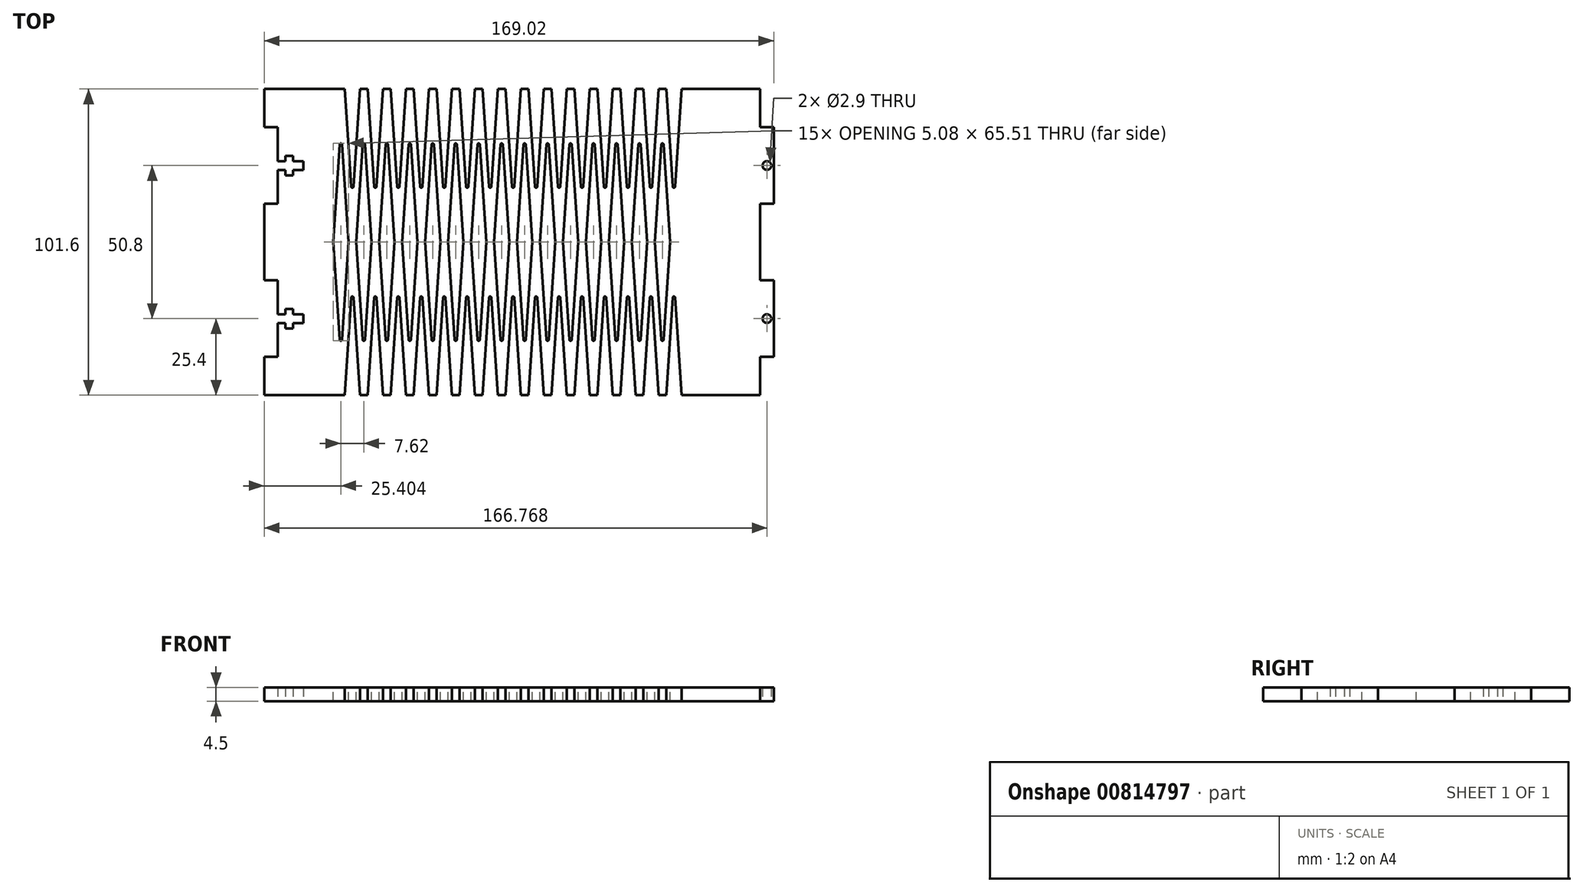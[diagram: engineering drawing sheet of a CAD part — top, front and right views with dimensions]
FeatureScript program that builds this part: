
annotation { "Feature Type Name" : "Feature", "Feature Type Description" : "" }
export const myFeature = defineFeature(function(context is Context, id is Id, definition is map)
    precondition{}
    {
        {
            var Q0;
            Q0=qCreatedBy(makeId("Top.planeOp"),FACE);
            var sketch = newSketch(context, id + "F0", { "sketchPlane" : qUnion([Q0])});
            skLineSegment(sketch, "E0.bottom", {"start": v(-80, 50.8) * mm, "end": v(80.01, 50.8) * mm});
            skLineSegment(sketch, "E0.top", {"start": v(-80, -50.8) * mm, "end": v(80.01, -50.8) * mm});
            skLineSegment(sketch, "E1", {"start": v(-80.01, 50.8) * mm, "end": v(80.01, -50.8) * mm, "construction": true});
            skLineSegment(sketch, "E2.left", {"start": v(-80, 38.1) * mm, "end": v(-80, 26.85) * mm});
            skLineSegment(sketch, "E3", {"start": v(-80, 50.8) * mm, "end": v(-84.5, 50.8) * mm});
            skLineSegment(sketch, "E4", {"start": v(-84.5, 50.8) * mm, "end": v(-84.5, 38.1) * mm});
            skLineSegment(sketch, "E5", {"start": v(-84.5, 38.1) * mm, "end": v(-80, 38.1) * mm});
            skLineSegment(sketch, "E6", {"start": v(-80, 12.7) * mm, "end": v(-84.5, 12.7) * mm});
            skLineSegment(sketch, "E7", {"start": v(-84.5, 12.7) * mm, "end": v(-84.5, 0) * mm});
            skLineSegment(sketch, "E8", {"start": v(-80, 26.85) * mm, "end": v(-77.47, 26.85) * mm});
            skLineSegment(sketch, "E9", {"start": v(-77.47, 26.85) * mm, "end": v(-77.47, 28.64) * mm});
            skLineSegment(sketch, "E10", {"start": v(-77.47, 28.64) * mm, "end": v(-74.96, 28.64) * mm});
            skLineSegment(sketch, "E11", {"start": v(-74.96, 28.64) * mm, "end": v(-74.96, 26.85) * mm});
            skLineSegment(sketch, "E12", {"start": v(-74.96, 26.85) * mm, "end": v(-71.55, 26.85) * mm});
            skLineSegment(sketch, "E13", {"start": v(-71.55, 26.85) * mm, "end": v(-71.55, 23.95) * mm});
            skLineSegment(sketch, "E14", {"start": v(-71.55, 23.95) * mm, "end": v(-74.96, 23.95) * mm});
            skLineSegment(sketch, "E15", {"start": v(-74.96, 23.95) * mm, "end": v(-74.96, 22.16) * mm});
            skLineSegment(sketch, "E16", {"start": v(-74.96, 22.16) * mm, "end": v(-77.47, 22.16) * mm});
            skLineSegment(sketch, "E17", {"start": v(-77.47, 22.16) * mm, "end": v(-77.47, 23.95) * mm});
            skLineSegment(sketch, "E18", {"start": v(-77.47, 23.95) * mm, "end": v(-80, 23.95) * mm});
            skLineSegment(sketch, "E19", {"start": v(-77.47, 26.85) * mm, "end": v(-77.47, 23.95) * mm, "construction": true});
            skLineSegment(sketch, "E20", {"start": v(-74.96, 26.85) * mm, "end": v(-74.96, 23.95) * mm, "construction": true});
            skLineSegment(sketch, "E21", {"start": v(-71.55, 25.4) * mm, "end": v(-80, 25.4) * mm, "construction": true});
            skPoint(sketch, "E21.endSnap0", {"position": v(-74.96, 25.4) * mm});
            skLineSegment(sketch, "E22", {"start": v(-80, 23.95) * mm, "end": v(-80, 12.7) * mm});
            skLineSegment(sketch, "E23", {"start": v(-80, 23.95) * mm, "end": v(-80, 26.85) * mm, "construction": true});
            skLineSegment(sketch, "E24", {"start": v(0, 0) * mm, "end": v(-84.5, 0) * mm, "construction": true});
            skLineSegment(sketch, "E25.MirrorCS", {"start": v(-77.47, -26.85) * mm, "end": v(-77.47, -28.64) * mm});
            skLineSegment(sketch, "E26.MirrorCS", {"start": v(-77.47, -28.64) * mm, "end": v(-74.96, -28.64) * mm});
            skLineSegment(sketch, "E27.MirrorCS", {"start": v(-74.96, -28.64) * mm, "end": v(-74.96, -26.85) * mm});
            skLineSegment(sketch, "E28.MirrorCS", {"start": v(-80, -26.85) * mm, "end": v(-77.47, -26.85) * mm});
            skLineSegment(sketch, "E29.MirrorCS", {"start": v(-71.55, -23.95) * mm, "end": v(-74.96, -23.95) * mm});
            skLineSegment(sketch, "E30.MirrorCS", {"start": v(-74.96, -26.85) * mm, "end": v(-74.96, -23.95) * mm, "construction": true});
            skLineSegment(sketch, "E31.MirrorCS", {"start": v(-77.47, -23.95) * mm, "end": v(-80, -23.95) * mm});
            skLineSegment(sketch, "E32.MirrorCS", {"start": v(-71.55, -25.4) * mm, "end": v(-80, -25.4) * mm, "construction": true});
            skLineSegment(sketch, "E33.MirrorCS", {"start": v(-74.96, -23.95) * mm, "end": v(-74.96, -22.16) * mm});
            skLineSegment(sketch, "E34.MirrorCS", {"start": v(-77.47, -22.16) * mm, "end": v(-77.47, -23.95) * mm});
            skLineSegment(sketch, "E35.MirrorCS", {"start": v(-80, -23.95) * mm, "end": v(-80, -26.85) * mm, "construction": true});
            skLineSegment(sketch, "E36.MirrorCS", {"start": v(-77.47, -26.85) * mm, "end": v(-77.47, -23.95) * mm, "construction": true});
            skLineSegment(sketch, "E37.MirrorCS", {"start": v(-74.96, -26.85) * mm, "end": v(-71.55, -26.85) * mm});
            skLineSegment(sketch, "E38.MirrorCS", {"start": v(-71.55, -26.85) * mm, "end": v(-71.55, -23.95) * mm});
            skLineSegment(sketch, "E39.MirrorCS", {"start": v(-74.96, -22.16) * mm, "end": v(-77.47, -22.16) * mm});
            skLineSegment(sketch, "E40.MirrorCS", {"start": v(-80, -12.7) * mm, "end": v(-84.5, -12.7) * mm});
            skLineSegment(sketch, "E41.MirrorCS", {"start": v(-84.5, -38.1) * mm, "end": v(-80, -38.1) * mm});
            skLineSegment(sketch, "E42.MirrorCS", {"start": v(-80, -50.8) * mm, "end": v(-84.5, -50.8) * mm});
            skLineSegment(sketch, "E43.MirrorCS", {"start": v(-84.5, -12.7) * mm, "end": v(-84.5, 0) * mm});
            skLineSegment(sketch, "E44.MirrorCS", {"start": v(-80, -23.95) * mm, "end": v(-80, -12.7) * mm});
            skPoint(sketch, "E45.MirrorP", {"position": v(-74.96, -25.4) * mm});
            skLineSegment(sketch, "E46.MirrorCS", {"start": v(-84.5, -50.8) * mm, "end": v(-84.5, -38.1) * mm});
            skLineSegment(sketch, "E47.MirrorCS", {"start": v(-80, -38.1) * mm, "end": v(-80, -26.85) * mm});
            skLineSegment(sketch, "E48.MirrorCS", {"start": v(80.01, 50.8) * mm, "end": v(80.01, 38.1) * mm});
            skLineSegment(sketch, "E49", {"start": v(80.01, 38.1) * mm, "end": v(84.5, 38.1) * mm});
            skLineSegment(sketch, "E50", {"start": v(84.5, 38.1) * mm, "end": v(84.5, 12.7) * mm});
            skLineSegment(sketch, "E51", {"start": v(84.5, 12.7) * mm, "end": v(80.01, 12.7) * mm});
            skLineSegment(sketch, "E52", {"start": v(80.01, 12.7) * mm, "end": v(80.01, 0) * mm});
            skCircle(sketch, "E53", {"center": v(82.26, 25.4) * mm, "radius": 1.45 * mm});
            skPoint(sketch, "E53.centerSnap0", {"position": v(84.5, 25.4) * mm});
            skLineSegment(sketch, "E54", {"start": v(0, 0) * mm, "end": v(80, 0) * mm, "construction": true});
            skLineSegment(sketch, "E55", {"start": v(84.5, 38.1) * mm, "end": v(80.01, 12.7) * mm, "construction": true});
            skLineSegment(sketch, "E56.MirrorCS", {"start": v(80.01, -38.1) * mm, "end": v(84.5, -38.1) * mm});
            skLineSegment(sketch, "E57.MirrorCS", {"start": v(84.5, -12.7) * mm, "end": v(80.01, -12.7) * mm});
            skCircle(sketch, "E58.MirrorC", {"center": v(82.26, -25.4) * mm, "radius": 1.45 * mm});
            skLineSegment(sketch, "E59.MirrorCS", {"start": v(80.01, -12.7) * mm, "end": v(80.01, 0) * mm});
            skLineSegment(sketch, "E60.MirrorCS", {"start": v(80.01, -50.8) * mm, "end": v(80.01, -38.1) * mm});
            skPoint(sketch, "E61.MirrorP", {"position": v(84.5, -25.4) * mm});
            skLineSegment(sketch, "E62.MirrorCS", {"start": v(84.5, -38.1) * mm, "end": v(84.5, -12.7) * mm});
            skSolve(sketch);
        }
        {
            var Q0;
            Q0 = qSketchRegion(id + "F0", true);
            extrude(context, id + "F1", {"entities" : qUnion([Q0]), "depth" : 4.5 * mm, "offsetDistance" : 25.4 * mm});
        }
        {
            var Q0;
            Q0=makeQuery(id+"F1.opExtrude","CAP_FACE",FACE,{"disambiguationData":[OSD([sQuery(id+"F0.wireOp",EDGE,"E0.bottom"),sQuery(id+"F0.wireOp",EDGE,"E0.top"),sQuery(id+"F0.wireOp",EDGE,"E2.left"),sQuery(id+"F0.wireOp",EDGE,"E3"),sQuery(id+"F0.wireOp",EDGE,"E4"),sQuery(id+"F0.wireOp",EDGE,"E5"),sQuery(id+"F0.wireOp",EDGE,"E6"),sQuery(id+"F0.wireOp",EDGE,"E7"),sQuery(id+"F0.wireOp",EDGE,"E8"),sQuery(id+"F0.wireOp",EDGE,"E9"),sQuery(id+"F0.wireOp",EDGE,"E10"),sQuery(id+"F0.wireOp",EDGE,"E11"),sQuery(id+"F0.wireOp",EDGE,"E12"),sQuery(id+"F0.wireOp",EDGE,"E13"),sQuery(id+"F0.wireOp",EDGE,"E14"),sQuery(id+"F0.wireOp",EDGE,"E15"),sQuery(id+"F0.wireOp",EDGE,"E16"),sQuery(id+"F0.wireOp",EDGE,"E17"),sQuery(id+"F0.wireOp",EDGE,"E18"),sQuery(id+"F0.wireOp",EDGE,"E22"),sQuery(id+"F0.wireOp",EDGE,"E25.MirrorCS"),sQuery(id+"F0.wireOp",EDGE,"E26.MirrorCS"),sQuery(id+"F0.wireOp",EDGE,"E27.MirrorCS"),sQuery(id+"F0.wireOp",EDGE,"E28.MirrorCS"),sQuery(id+"F0.wireOp",EDGE,"E29.MirrorCS"),sQuery(id+"F0.wireOp",EDGE,"E31.MirrorCS"),sQuery(id+"F0.wireOp",EDGE,"E33.MirrorCS"),sQuery(id+"F0.wireOp",EDGE,"E34.MirrorCS"),sQuery(id+"F0.wireOp",EDGE,"E37.MirrorCS"),sQuery(id+"F0.wireOp",EDGE,"E38.MirrorCS"),sQuery(id+"F0.wireOp",EDGE,"E39.MirrorCS"),sQuery(id+"F0.wireOp",EDGE,"E40.MirrorCS"),sQuery(id+"F0.wireOp",EDGE,"E41.MirrorCS"),sQuery(id+"F0.wireOp",EDGE,"E42.MirrorCS"),sQuery(id+"F0.wireOp",EDGE,"E43.MirrorCS"),sQuery(id+"F0.wireOp",EDGE,"E44.MirrorCS"),sQuery(id+"F0.wireOp",EDGE,"E46.MirrorCS"),sQuery(id+"F0.wireOp",EDGE,"E47.MirrorCS"),sQuery(id+"F0.wireOp",EDGE,"E48.MirrorCS"),sQuery(id+"F0.wireOp",EDGE,"E49"),sQuery(id+"F0.wireOp",EDGE,"E50"),sQuery(id+"F0.wireOp",EDGE,"E51"),sQuery(id+"F0.wireOp",EDGE,"E52"),sQuery(id+"F0.wireOp",EDGE,"E53"),sQuery(id+"F0.wireOp",EDGE,"E56.MirrorCS"),sQuery(id+"F0.wireOp",EDGE,"E57.MirrorCS"),sQuery(id+"F0.wireOp",EDGE,"E58.MirrorC"),sQuery(id+"F0.wireOp",EDGE,"E59.MirrorCS"),sQuery(id+"F0.wireOp",EDGE,"E60.MirrorCS"),sQuery(id+"F0.wireOp",EDGE,"E62.MirrorCS")])],"isStart":false});
            var sketch = newSketch(context, id + "F2", { "sketchPlane" : qUnion([Q0])});
            skLineSegment(sketch, "E63", {"start": v(-59.49, 32.4) * mm, "end": v(-61.65, 0) * mm});
            skLineSegment(sketch, "E64", {"start": v(-61.65, 0) * mm, "end": v(-56.57, 0) * mm, "construction": true});
            skLineSegment(sketch, "E65", {"start": v(-56.57, 0) * mm, "end": v(-58.73, 32.4) * mm});
            skLineSegment(sketch, "E66", {"start": v(-57.84, 50.8) * mm, "end": v(-55.68, 18.4) * mm});
            skLineSegment(sketch, "E67", {"start": v(-54.92, 18.4) * mm, "end": v(-52.76, 50.8) * mm});
            skLineSegment(sketch, "E68", {"start": v(-52.76, 50.8) * mm, "end": v(-57.84, 50.8) * mm});
            skLineSegment(sketch, "E69", {"start": v(-59.1, 38.1) * mm, "end": v(-59.1, 0) * mm, "construction": true});
            skLineSegment(sketch, "E70", {"start": v(-55.3, 12.7) * mm, "end": v(-55.3, 50.8) * mm, "construction": true});
            skPoint(sketch, "E71.visualSharp", {"position": v(-59.1, 38.1) * mm});
            skArc(sketch, "E71.filletArc", {"start": v(-58.73, 32.4) * mm, "mid": v(-59.1, 32.75) * mm, "end": v(-59.49, 32.4) * mm});
            skPoint(sketch, "E72.visualSharp", {"position": v(-55.3, 12.7) * mm});
            skArc(sketch, "E72.filletArc", {"start": v(-55.68, 18.4) * mm, "mid": v(-55.3, 18.05) * mm, "end": v(-54.92, 18.4) * mm});
            skArc(sketch, "E73.MirrorCS", {"start": v(-55.68, -18.4) * mm, "mid": v(-55.3, -18.05) * mm, "end": v(-54.92, -18.4) * mm});
            skArc(sketch, "E74.MirrorCS", {"start": v(-58.73, -32.4) * mm, "mid": v(-59.1, -32.75) * mm, "end": v(-59.49, -32.4) * mm});
            skLineSegment(sketch, "E75.MirrorCS", {"start": v(-52.76, -50.8) * mm, "end": v(-57.84, -50.8) * mm});
            skLineSegment(sketch, "E76.MirrorCS", {"start": v(-57.84, -50.8) * mm, "end": v(-55.68, -18.4) * mm});
            skLineSegment(sketch, "E77.MirrorCS", {"start": v(-56.57, 0) * mm, "end": v(-58.73, -32.4) * mm});
            skPoint(sketch, "E78.MirrorP", {"position": v(-59.1, -38.1) * mm});
            skLineSegment(sketch, "E79.MirrorCS", {"start": v(-54.92, -18.4) * mm, "end": v(-52.76, -50.8) * mm});
            skPoint(sketch, "E80.MirrorP", {"position": v(-55.3, -12.7) * mm});
            skLineSegment(sketch, "E81.MirrorCS", {"start": v(-59.49, -32.4) * mm, "end": v(-61.65, 0) * mm});
            skLineSegment(sketch, "E82.1.0.0", {"start": v(-51.87, -32.4) * mm, "end": v(-54.03, 0) * mm});
            skPoint(sketch, "E82.1.0.1", {"position": v(-47.68, -12.7) * mm});
            skPoint(sketch, "E82.1.0.2", {"position": v(-51.49, -38.1) * mm});
            skLineSegment(sketch, "E82.1.0.3", {"start": v(-50.22, 50.8) * mm, "end": v(-48.06, 18.4) * mm});
            skLineSegment(sketch, "E82.1.0.4", {"start": v(-47.3, -18.4) * mm, "end": v(-45.14, -50.8) * mm});
            skLineSegment(sketch, "E82.1.0.5", {"start": v(-48.95, 0) * mm, "end": v(-51.1, -32.4) * mm});
            skPoint(sketch, "E82.1.0.6", {"position": v(-51.49, 38.1) * mm});
            skLineSegment(sketch, "E82.1.0.7", {"start": v(-48.95, 0) * mm, "end": v(-51.1, 32.4) * mm});
            skLineSegment(sketch, "E82.1.0.8", {"start": v(-51.49, 38.1) * mm, "end": v(-51.49, 0) * mm, "construction": true});
            skLineSegment(sketch, "E82.1.0.9", {"start": v(-47.3, 18.4) * mm, "end": v(-45.14, 50.8) * mm});
            skLineSegment(sketch, "E82.1.0.10", {"start": v(-51.87, 32.4) * mm, "end": v(-54.03, 0) * mm});
            skPoint(sketch, "E82.1.0.11", {"position": v(-47.68, 12.7) * mm});
            skLineSegment(sketch, "E82.1.0.12", {"start": v(-47.68, 12.7) * mm, "end": v(-47.68, 50.8) * mm, "construction": true});
            skLineSegment(sketch, "E82.1.0.13", {"start": v(-50.22, -50.8) * mm, "end": v(-48.06, -18.4) * mm});
            skLineSegment(sketch, "E82.1.0.14", {"start": v(-45.14, -50.8) * mm, "end": v(-50.22, -50.8) * mm});
            skArc(sketch, "E82.1.0.15", {"start": v(-48.06, -18.4) * mm, "mid": v(-47.68, -18.05) * mm, "end": v(-47.3, -18.4) * mm});
            skLineSegment(sketch, "E82.1.0.16", {"start": v(-54.03, 0) * mm, "end": v(-48.95, 0) * mm, "construction": true});
            skLineSegment(sketch, "E82.1.0.17", {"start": v(-45.14, 50.8) * mm, "end": v(-50.22, 50.8) * mm});
            skArc(sketch, "E82.1.0.18", {"start": v(-48.06, 18.4) * mm, "mid": v(-47.68, 18.05) * mm, "end": v(-47.3, 18.4) * mm});
            skArc(sketch, "E82.1.0.19", {"start": v(-51.1, -32.4) * mm, "mid": v(-51.49, -32.75) * mm, "end": v(-51.87, -32.4) * mm});
            skArc(sketch, "E82.1.0.20", {"start": v(-51.1, 32.4) * mm, "mid": v(-51.49, 32.75) * mm, "end": v(-51.87, 32.4) * mm});
            skLineSegment(sketch, "E82.2.0.0", {"start": v(-44.25, -32.4) * mm, "end": v(-46.4, 0) * mm});
            skPoint(sketch, "E82.2.0.1", {"position": v(-40.06, -12.7) * mm});
            skPoint(sketch, "E82.2.0.2", {"position": v(-43.87, -38.1) * mm});
            skLineSegment(sketch, "E82.2.0.3", {"start": v(-42.6, 50.8) * mm, "end": v(-40.44, 18.4) * mm});
            skLineSegment(sketch, "E82.2.0.4", {"start": v(-39.68, -18.4) * mm, "end": v(-37.52, -50.8) * mm});
            skLineSegment(sketch, "E82.2.0.5", {"start": v(-41.33, 0) * mm, "end": v(-43.49, -32.4) * mm});
            skPoint(sketch, "E82.2.0.6", {"position": v(-43.87, 38.1) * mm});
            skLineSegment(sketch, "E82.2.0.7", {"start": v(-41.33, 0) * mm, "end": v(-43.49, 32.4) * mm});
            skLineSegment(sketch, "E82.2.0.8", {"start": v(-43.87, 38.1) * mm, "end": v(-43.87, 0) * mm, "construction": true});
            skLineSegment(sketch, "E82.2.0.9", {"start": v(-39.68, 18.4) * mm, "end": v(-37.52, 50.8) * mm});
            skLineSegment(sketch, "E82.2.0.10", {"start": v(-44.25, 32.4) * mm, "end": v(-46.4, 0) * mm});
            skPoint(sketch, "E82.2.0.11", {"position": v(-40.06, 12.7) * mm});
            skLineSegment(sketch, "E82.2.0.12", {"start": v(-40.06, 12.7) * mm, "end": v(-40.06, 50.8) * mm, "construction": true});
            skLineSegment(sketch, "E82.2.0.13", {"start": v(-42.6, -50.8) * mm, "end": v(-40.44, -18.4) * mm});
            skLineSegment(sketch, "E82.2.0.14", {"start": v(-37.52, -50.8) * mm, "end": v(-42.6, -50.8) * mm});
            skArc(sketch, "E82.2.0.15", {"start": v(-40.44, -18.4) * mm, "mid": v(-40.06, -18.05) * mm, "end": v(-39.68, -18.4) * mm});
            skLineSegment(sketch, "E82.2.0.16", {"start": v(-46.4, 0) * mm, "end": v(-41.33, 0) * mm, "construction": true});
            skLineSegment(sketch, "E82.2.0.17", {"start": v(-37.52, 50.8) * mm, "end": v(-42.6, 50.8) * mm});
            skArc(sketch, "E82.2.0.18", {"start": v(-40.44, 18.4) * mm, "mid": v(-40.06, 18.05) * mm, "end": v(-39.68, 18.4) * mm});
            skArc(sketch, "E82.2.0.19", {"start": v(-43.49, -32.4) * mm, "mid": v(-43.87, -32.75) * mm, "end": v(-44.25, -32.4) * mm});
            skArc(sketch, "E82.2.0.20", {"start": v(-43.49, 32.4) * mm, "mid": v(-43.87, 32.75) * mm, "end": v(-44.25, 32.4) * mm});
            skLineSegment(sketch, "E82.3.0.0", {"start": v(-36.63, -32.4) * mm, "end": v(-38.79, 0) * mm});
            skPoint(sketch, "E82.3.0.1", {"position": v(-32.44, -12.7) * mm});
            skPoint(sketch, "E82.3.0.2", {"position": v(-36.25, -38.1) * mm});
            skLineSegment(sketch, "E82.3.0.3", {"start": v(-34.98, 50.8) * mm, "end": v(-32.82, 18.4) * mm});
            skLineSegment(sketch, "E82.3.0.4", {"start": v(-32.06, -18.4) * mm, "end": v(-29.9, -50.8) * mm});
            skLineSegment(sketch, "E82.3.0.5", {"start": v(-33.7, 0) * mm, "end": v(-35.87, -32.4) * mm});
            skPoint(sketch, "E82.3.0.6", {"position": v(-36.25, 38.1) * mm});
            skLineSegment(sketch, "E82.3.0.7", {"start": v(-33.7, 0) * mm, "end": v(-35.87, 32.4) * mm});
            skLineSegment(sketch, "E82.3.0.8", {"start": v(-36.25, 38.1) * mm, "end": v(-36.25, 0) * mm, "construction": true});
            skLineSegment(sketch, "E82.3.0.9", {"start": v(-32.06, 18.4) * mm, "end": v(-29.9, 50.8) * mm});
            skLineSegment(sketch, "E82.3.0.10", {"start": v(-36.63, 32.4) * mm, "end": v(-38.79, 0) * mm});
            skPoint(sketch, "E82.3.0.11", {"position": v(-32.44, 12.7) * mm});
            skLineSegment(sketch, "E82.3.0.12", {"start": v(-32.44, 12.7) * mm, "end": v(-32.44, 50.8) * mm, "construction": true});
            skLineSegment(sketch, "E82.3.0.13", {"start": v(-34.98, -50.8) * mm, "end": v(-32.82, -18.4) * mm});
            skLineSegment(sketch, "E82.3.0.14", {"start": v(-29.9, -50.8) * mm, "end": v(-34.98, -50.8) * mm});
            skArc(sketch, "E82.3.0.15", {"start": v(-32.82, -18.4) * mm, "mid": v(-32.44, -18.05) * mm, "end": v(-32.06, -18.4) * mm});
            skLineSegment(sketch, "E82.3.0.16", {"start": v(-38.79, 0) * mm, "end": v(-33.7, 0) * mm, "construction": true});
            skLineSegment(sketch, "E82.3.0.17", {"start": v(-29.9, 50.8) * mm, "end": v(-34.98, 50.8) * mm});
            skArc(sketch, "E82.3.0.18", {"start": v(-32.82, 18.4) * mm, "mid": v(-32.44, 18.05) * mm, "end": v(-32.06, 18.4) * mm});
            skArc(sketch, "E82.3.0.19", {"start": v(-35.87, -32.4) * mm, "mid": v(-36.25, -32.75) * mm, "end": v(-36.63, -32.4) * mm});
            skArc(sketch, "E82.3.0.20", {"start": v(-35.87, 32.4) * mm, "mid": v(-36.25, 32.75) * mm, "end": v(-36.63, 32.4) * mm});
            skLineSegment(sketch, "E82.4.0.0", {"start": v(-29, -32.4) * mm, "end": v(-31.17, 0) * mm});
            skPoint(sketch, "E82.4.0.1", {"position": v(-24.82, -12.7) * mm});
            skPoint(sketch, "E82.4.0.2", {"position": v(-28.63, -38.1) * mm});
            skLineSegment(sketch, "E82.4.0.3", {"start": v(-27.36, 50.8) * mm, "end": v(-25.2, 18.4) * mm});
            skLineSegment(sketch, "E82.4.0.4", {"start": v(-24.44, -18.4) * mm, "end": v(-22.28, -50.8) * mm});
            skLineSegment(sketch, "E82.4.0.5", {"start": v(-26.09, 0) * mm, "end": v(-28.25, -32.4) * mm});
            skPoint(sketch, "E82.4.0.6", {"position": v(-28.63, 38.1) * mm});
            skLineSegment(sketch, "E82.4.0.7", {"start": v(-26.09, 0) * mm, "end": v(-28.25, 32.4) * mm});
            skLineSegment(sketch, "E82.4.0.8", {"start": v(-28.63, 38.1) * mm, "end": v(-28.63, 0) * mm, "construction": true});
            skLineSegment(sketch, "E82.4.0.9", {"start": v(-24.44, 18.4) * mm, "end": v(-22.28, 50.8) * mm});
            skLineSegment(sketch, "E82.4.0.10", {"start": v(-29, 32.4) * mm, "end": v(-31.17, 0) * mm});
            skPoint(sketch, "E82.4.0.11", {"position": v(-24.82, 12.7) * mm});
            skLineSegment(sketch, "E82.4.0.12", {"start": v(-24.82, 12.7) * mm, "end": v(-24.82, 50.8) * mm, "construction": true});
            skLineSegment(sketch, "E82.4.0.13", {"start": v(-27.36, -50.8) * mm, "end": v(-25.2, -18.4) * mm});
            skLineSegment(sketch, "E82.4.0.14", {"start": v(-22.28, -50.8) * mm, "end": v(-27.36, -50.8) * mm});
            skArc(sketch, "E82.4.0.15", {"start": v(-25.2, -18.4) * mm, "mid": v(-24.82, -18.05) * mm, "end": v(-24.44, -18.4) * mm});
            skLineSegment(sketch, "E82.4.0.16", {"start": v(-31.17, 0) * mm, "end": v(-26.09, 0) * mm, "construction": true});
            skLineSegment(sketch, "E82.4.0.17", {"start": v(-22.28, 50.8) * mm, "end": v(-27.36, 50.8) * mm});
            skArc(sketch, "E82.4.0.18", {"start": v(-25.2, 18.4) * mm, "mid": v(-24.82, 18.05) * mm, "end": v(-24.44, 18.4) * mm});
            skArc(sketch, "E82.4.0.19", {"start": v(-28.25, -32.4) * mm, "mid": v(-28.63, -32.75) * mm, "end": v(-29, -32.4) * mm});
            skArc(sketch, "E82.4.0.20", {"start": v(-28.25, 32.4) * mm, "mid": v(-28.63, 32.75) * mm, "end": v(-29, 32.4) * mm});
            skLineSegment(sketch, "E82.5.0.0", {"start": v(-21.39, -32.4) * mm, "end": v(-23.55, 0) * mm});
            skPoint(sketch, "E82.5.0.1", {"position": v(-17.2, -12.7) * mm});
            skPoint(sketch, "E82.5.0.2", {"position": v(-21, -38.1) * mm});
            skLineSegment(sketch, "E82.5.0.3", {"start": v(-19.74, 50.8) * mm, "end": v(-17.58, 18.4) * mm});
            skLineSegment(sketch, "E82.5.0.4", {"start": v(-16.82, -18.4) * mm, "end": v(-14.66, -50.8) * mm});
            skLineSegment(sketch, "E82.5.0.5", {"start": v(-18.47, 0) * mm, "end": v(-20.63, -32.4) * mm});
            skPoint(sketch, "E82.5.0.6", {"position": v(-21, 38.1) * mm});
            skLineSegment(sketch, "E82.5.0.7", {"start": v(-18.47, 0) * mm, "end": v(-20.63, 32.4) * mm});
            skLineSegment(sketch, "E82.5.0.8", {"start": v(-21, 38.1) * mm, "end": v(-21, 0) * mm, "construction": true});
            skLineSegment(sketch, "E82.5.0.9", {"start": v(-16.82, 18.4) * mm, "end": v(-14.66, 50.8) * mm});
            skLineSegment(sketch, "E82.5.0.10", {"start": v(-21.39, 32.4) * mm, "end": v(-23.55, 0) * mm});
            skPoint(sketch, "E82.5.0.11", {"position": v(-17.2, 12.7) * mm});
            skLineSegment(sketch, "E82.5.0.12", {"start": v(-17.2, 12.7) * mm, "end": v(-17.2, 50.8) * mm, "construction": true});
            skLineSegment(sketch, "E82.5.0.13", {"start": v(-19.74, -50.8) * mm, "end": v(-17.58, -18.4) * mm});
            skLineSegment(sketch, "E82.5.0.14", {"start": v(-14.66, -50.8) * mm, "end": v(-19.74, -50.8) * mm});
            skArc(sketch, "E82.5.0.15", {"start": v(-17.58, -18.4) * mm, "mid": v(-17.2, -18.05) * mm, "end": v(-16.82, -18.4) * mm});
            skLineSegment(sketch, "E82.5.0.16", {"start": v(-23.55, 0) * mm, "end": v(-18.47, 0) * mm, "construction": true});
            skLineSegment(sketch, "E82.5.0.17", {"start": v(-14.66, 50.8) * mm, "end": v(-19.74, 50.8) * mm});
            skArc(sketch, "E82.5.0.18", {"start": v(-17.58, 18.4) * mm, "mid": v(-17.2, 18.05) * mm, "end": v(-16.82, 18.4) * mm});
            skArc(sketch, "E82.5.0.19", {"start": v(-20.63, -32.4) * mm, "mid": v(-21, -32.75) * mm, "end": v(-21.39, -32.4) * mm});
            skArc(sketch, "E82.5.0.20", {"start": v(-20.63, 32.4) * mm, "mid": v(-21, 32.75) * mm, "end": v(-21.39, 32.4) * mm});
            skLineSegment(sketch, "E82.6.0.0", {"start": v(-13.77, -32.4) * mm, "end": v(-15.93, 0) * mm});
            skPoint(sketch, "E82.6.0.1", {"position": v(-9.58, -12.7) * mm});
            skPoint(sketch, "E82.6.0.2", {"position": v(-13.39, -38.1) * mm});
            skLineSegment(sketch, "E82.6.0.3", {"start": v(-12.12, 50.8) * mm, "end": v(-9.96, 18.4) * mm});
            skLineSegment(sketch, "E82.6.0.4", {"start": v(-9.2, -18.4) * mm, "end": v(-7.04, -50.8) * mm});
            skLineSegment(sketch, "E82.6.0.5", {"start": v(-10.85, 0) * mm, "end": v(-13, -32.4) * mm});
            skPoint(sketch, "E82.6.0.6", {"position": v(-13.39, 38.1) * mm});
            skLineSegment(sketch, "E82.6.0.7", {"start": v(-10.85, 0) * mm, "end": v(-13, 32.4) * mm});
            skLineSegment(sketch, "E82.6.0.8", {"start": v(-13.39, 38.1) * mm, "end": v(-13.39, 0) * mm, "construction": true});
            skLineSegment(sketch, "E82.6.0.9", {"start": v(-9.2, 18.4) * mm, "end": v(-7.04, 50.8) * mm});
            skLineSegment(sketch, "E82.6.0.10", {"start": v(-13.77, 32.4) * mm, "end": v(-15.93, 0) * mm});
            skPoint(sketch, "E82.6.0.11", {"position": v(-9.58, 12.7) * mm});
            skLineSegment(sketch, "E82.6.0.12", {"start": v(-9.58, 12.7) * mm, "end": v(-9.58, 50.8) * mm, "construction": true});
            skLineSegment(sketch, "E82.6.0.13", {"start": v(-12.12, -50.8) * mm, "end": v(-9.96, -18.4) * mm});
            skLineSegment(sketch, "E82.6.0.14", {"start": v(-7.04, -50.8) * mm, "end": v(-12.12, -50.8) * mm});
            skArc(sketch, "E82.6.0.15", {"start": v(-9.96, -18.4) * mm, "mid": v(-9.58, -18.05) * mm, "end": v(-9.2, -18.4) * mm});
            skLineSegment(sketch, "E82.6.0.16", {"start": v(-15.93, 0) * mm, "end": v(-10.85, 0) * mm, "construction": true});
            skLineSegment(sketch, "E82.6.0.17", {"start": v(-7.04, 50.8) * mm, "end": v(-12.12, 50.8) * mm});
            skArc(sketch, "E82.6.0.18", {"start": v(-9.96, 18.4) * mm, "mid": v(-9.58, 18.05) * mm, "end": v(-9.2, 18.4) * mm});
            skArc(sketch, "E82.6.0.19", {"start": v(-13, -32.4) * mm, "mid": v(-13.39, -32.75) * mm, "end": v(-13.77, -32.4) * mm});
            skArc(sketch, "E82.6.0.20", {"start": v(-13, 32.4) * mm, "mid": v(-13.39, 32.75) * mm, "end": v(-13.77, 32.4) * mm});
            skLineSegment(sketch, "E82.7.0.0", {"start": v(-6.15, -32.4) * mm, "end": v(-8.3, 0) * mm});
            skPoint(sketch, "E82.7.0.1", {"position": v(-1.96, -12.7) * mm});
            skPoint(sketch, "E82.7.0.2", {"position": v(-5.77, -38.1) * mm});
            skLineSegment(sketch, "E82.7.0.3", {"start": v(-4.5, 50.8) * mm, "end": v(-2.34, 18.4) * mm});
            skLineSegment(sketch, "E82.7.0.4", {"start": v(-1.58, -18.4) * mm, "end": v(0.58, -50.8) * mm});
            skLineSegment(sketch, "E82.7.0.5", {"start": v(-3.23, 0) * mm, "end": v(-5.39, -32.4) * mm});
            skPoint(sketch, "E82.7.0.6", {"position": v(-5.77, 38.1) * mm});
            skLineSegment(sketch, "E82.7.0.7", {"start": v(-3.23, 0) * mm, "end": v(-5.39, 32.4) * mm});
            skLineSegment(sketch, "E82.7.0.8", {"start": v(-5.77, 38.1) * mm, "end": v(-5.77, 0) * mm, "construction": true});
            skLineSegment(sketch, "E82.7.0.9", {"start": v(-1.58, 18.4) * mm, "end": v(0.58, 50.8) * mm});
            skLineSegment(sketch, "E82.7.0.10", {"start": v(-6.15, 32.4) * mm, "end": v(-8.3, 0) * mm});
            skPoint(sketch, "E82.7.0.11", {"position": v(-1.96, 12.7) * mm});
            skLineSegment(sketch, "E82.7.0.12", {"start": v(-1.96, 12.7) * mm, "end": v(-1.96, 50.8) * mm, "construction": true});
            skLineSegment(sketch, "E82.7.0.13", {"start": v(-4.5, -50.8) * mm, "end": v(-2.34, -18.4) * mm});
            skLineSegment(sketch, "E82.7.0.14", {"start": v(0.58, -50.8) * mm, "end": v(-4.5, -50.8) * mm});
            skArc(sketch, "E82.7.0.15", {"start": v(-2.34, -18.4) * mm, "mid": v(-1.96, -18.05) * mm, "end": v(-1.58, -18.4) * mm});
            skLineSegment(sketch, "E82.7.0.16", {"start": v(-8.3, 0) * mm, "end": v(-3.23, 0) * mm, "construction": true});
            skLineSegment(sketch, "E82.7.0.17", {"start": v(0.58, 50.8) * mm, "end": v(-4.5, 50.8) * mm});
            skArc(sketch, "E82.7.0.18", {"start": v(-2.34, 18.4) * mm, "mid": v(-1.96, 18.05) * mm, "end": v(-1.58, 18.4) * mm});
            skArc(sketch, "E82.7.0.19", {"start": v(-5.39, -32.4) * mm, "mid": v(-5.77, -32.75) * mm, "end": v(-6.15, -32.4) * mm});
            skArc(sketch, "E82.7.0.20", {"start": v(-5.39, 32.4) * mm, "mid": v(-5.77, 32.75) * mm, "end": v(-6.15, 32.4) * mm});
            skLineSegment(sketch, "E82.8.0.0", {"start": v(1.47, -32.4) * mm, "end": v(-0.69, 0) * mm});
            skPoint(sketch, "E82.8.0.1", {"position": v(5.66, -12.7) * mm});
            skPoint(sketch, "E82.8.0.2", {"position": v(1.85, -38.1) * mm});
            skLineSegment(sketch, "E82.8.0.3", {"start": v(3.12, 50.8) * mm, "end": v(5.28, 18.4) * mm});
            skLineSegment(sketch, "E82.8.0.4", {"start": v(6.04, -18.4) * mm, "end": v(8.2, -50.8) * mm});
            skLineSegment(sketch, "E82.8.0.5", {"start": v(4.4, 0) * mm, "end": v(2.23, -32.4) * mm});
            skPoint(sketch, "E82.8.0.6", {"position": v(1.85, 38.1) * mm});
            skLineSegment(sketch, "E82.8.0.7", {"start": v(4.4, 0) * mm, "end": v(2.23, 32.4) * mm});
            skLineSegment(sketch, "E82.8.0.8", {"start": v(1.85, 38.1) * mm, "end": v(1.85, 0) * mm, "construction": true});
            skLineSegment(sketch, "E82.8.0.9", {"start": v(6.04, 18.4) * mm, "end": v(8.2, 50.8) * mm});
            skLineSegment(sketch, "E82.8.0.10", {"start": v(1.47, 32.4) * mm, "end": v(-0.69, 0) * mm});
            skPoint(sketch, "E82.8.0.11", {"position": v(5.66, 12.7) * mm});
            skLineSegment(sketch, "E82.8.0.12", {"start": v(5.66, 12.7) * mm, "end": v(5.66, 50.8) * mm, "construction": true});
            skLineSegment(sketch, "E82.8.0.13", {"start": v(3.12, -50.8) * mm, "end": v(5.28, -18.4) * mm});
            skLineSegment(sketch, "E82.8.0.14", {"start": v(8.2, -50.8) * mm, "end": v(3.12, -50.8) * mm});
            skArc(sketch, "E82.8.0.15", {"start": v(5.28, -18.4) * mm, "mid": v(5.66, -18.05) * mm, "end": v(6.04, -18.4) * mm});
            skLineSegment(sketch, "E82.8.0.16", {"start": v(-0.69, 0) * mm, "end": v(4.4, 0) * mm, "construction": true});
            skLineSegment(sketch, "E82.8.0.17", {"start": v(8.2, 50.8) * mm, "end": v(3.12, 50.8) * mm});
            skArc(sketch, "E82.8.0.18", {"start": v(5.28, 18.4) * mm, "mid": v(5.66, 18.05) * mm, "end": v(6.04, 18.4) * mm});
            skArc(sketch, "E82.8.0.19", {"start": v(2.23, -32.4) * mm, "mid": v(1.85, -32.75) * mm, "end": v(1.47, -32.4) * mm});
            skArc(sketch, "E82.8.0.20", {"start": v(2.23, 32.4) * mm, "mid": v(1.85, 32.75) * mm, "end": v(1.47, 32.4) * mm});
            skLineSegment(sketch, "E82.9.0.0", {"start": v(9.1, -32.4) * mm, "end": v(6.93, 0) * mm});
            skPoint(sketch, "E82.9.0.1", {"position": v(13.28, -12.7) * mm});
            skPoint(sketch, "E82.9.0.2", {"position": v(9.47, -38.1) * mm});
            skLineSegment(sketch, "E82.9.0.3", {"start": v(10.74, 50.8) * mm, "end": v(12.9, 18.4) * mm});
            skLineSegment(sketch, "E82.9.0.4", {"start": v(13.66, -18.4) * mm, "end": v(15.82, -50.8) * mm});
            skLineSegment(sketch, "E82.9.0.5", {"start": v(12.01, 0) * mm, "end": v(9.85, -32.4) * mm});
            skPoint(sketch, "E82.9.0.6", {"position": v(9.47, 38.1) * mm});
            skLineSegment(sketch, "E82.9.0.7", {"start": v(12.01, 0) * mm, "end": v(9.85, 32.4) * mm});
            skLineSegment(sketch, "E82.9.0.8", {"start": v(9.47, 38.1) * mm, "end": v(9.47, 0) * mm, "construction": true});
            skLineSegment(sketch, "E82.9.0.9", {"start": v(13.66, 18.4) * mm, "end": v(15.82, 50.8) * mm});
            skLineSegment(sketch, "E82.9.0.10", {"start": v(9.1, 32.4) * mm, "end": v(6.93, 0) * mm});
            skPoint(sketch, "E82.9.0.11", {"position": v(13.28, 12.7) * mm});
            skLineSegment(sketch, "E82.9.0.12", {"start": v(13.28, 12.7) * mm, "end": v(13.28, 50.8) * mm, "construction": true});
            skLineSegment(sketch, "E82.9.0.13", {"start": v(10.74, -50.8) * mm, "end": v(12.9, -18.4) * mm});
            skLineSegment(sketch, "E82.9.0.14", {"start": v(15.82, -50.8) * mm, "end": v(10.74, -50.8) * mm});
            skArc(sketch, "E82.9.0.15", {"start": v(12.9, -18.4) * mm, "mid": v(13.28, -18.05) * mm, "end": v(13.66, -18.4) * mm});
            skLineSegment(sketch, "E82.9.0.16", {"start": v(6.93, 0) * mm, "end": v(12.01, 0) * mm, "construction": true});
            skLineSegment(sketch, "E82.9.0.17", {"start": v(15.82, 50.8) * mm, "end": v(10.74, 50.8) * mm});
            skArc(sketch, "E82.9.0.18", {"start": v(12.9, 18.4) * mm, "mid": v(13.28, 18.05) * mm, "end": v(13.66, 18.4) * mm});
            skArc(sketch, "E82.9.0.19", {"start": v(9.85, -32.4) * mm, "mid": v(9.47, -32.75) * mm, "end": v(9.1, -32.4) * mm});
            skArc(sketch, "E82.9.0.20", {"start": v(9.85, 32.4) * mm, "mid": v(9.47, 32.75) * mm, "end": v(9.1, 32.4) * mm});
            skLineSegment(sketch, "E82.10.0.0", {"start": v(16.71, -32.4) * mm, "end": v(14.55, 0) * mm});
            skPoint(sketch, "E82.10.0.1", {"position": v(20.9, -12.7) * mm});
            skPoint(sketch, "E82.10.0.2", {"position": v(17.1, -38.1) * mm});
            skLineSegment(sketch, "E82.10.0.3", {"start": v(18.36, 50.8) * mm, "end": v(20.52, 18.4) * mm});
            skLineSegment(sketch, "E82.10.0.4", {"start": v(21.28, -18.4) * mm, "end": v(23.44, -50.8) * mm});
            skLineSegment(sketch, "E82.10.0.5", {"start": v(19.63, 0) * mm, "end": v(17.47, -32.4) * mm});
            skPoint(sketch, "E82.10.0.6", {"position": v(17.1, 38.1) * mm});
            skLineSegment(sketch, "E82.10.0.7", {"start": v(19.63, 0) * mm, "end": v(17.47, 32.4) * mm});
            skLineSegment(sketch, "E82.10.0.8", {"start": v(17.1, 38.1) * mm, "end": v(17.1, 0) * mm, "construction": true});
            skLineSegment(sketch, "E82.10.0.9", {"start": v(21.28, 18.4) * mm, "end": v(23.44, 50.8) * mm});
            skLineSegment(sketch, "E82.10.0.10", {"start": v(16.71, 32.4) * mm, "end": v(14.55, 0) * mm});
            skPoint(sketch, "E82.10.0.11", {"position": v(20.9, 12.7) * mm});
            skLineSegment(sketch, "E82.10.0.12", {"start": v(20.9, 12.7) * mm, "end": v(20.9, 50.8) * mm, "construction": true});
            skLineSegment(sketch, "E82.10.0.13", {"start": v(18.36, -50.8) * mm, "end": v(20.52, -18.4) * mm});
            skLineSegment(sketch, "E82.10.0.14", {"start": v(23.44, -50.8) * mm, "end": v(18.36, -50.8) * mm});
            skArc(sketch, "E82.10.0.15", {"start": v(20.52, -18.4) * mm, "mid": v(20.9, -18.05) * mm, "end": v(21.28, -18.4) * mm});
            skLineSegment(sketch, "E82.10.0.16", {"start": v(14.55, 0) * mm, "end": v(19.63, 0) * mm, "construction": true});
            skLineSegment(sketch, "E82.10.0.17", {"start": v(23.44, 50.8) * mm, "end": v(18.36, 50.8) * mm});
            skArc(sketch, "E82.10.0.18", {"start": v(20.52, 18.4) * mm, "mid": v(20.9, 18.05) * mm, "end": v(21.28, 18.4) * mm});
            skArc(sketch, "E82.10.0.19", {"start": v(17.47, -32.4) * mm, "mid": v(17.1, -32.75) * mm, "end": v(16.71, -32.4) * mm});
            skArc(sketch, "E82.10.0.20", {"start": v(17.47, 32.4) * mm, "mid": v(17.1, 32.75) * mm, "end": v(16.71, 32.4) * mm});
            skLineSegment(sketch, "E82.11.0.0", {"start": v(24.33, -32.4) * mm, "end": v(22.17, 0) * mm});
            skPoint(sketch, "E82.11.0.1", {"position": v(28.52, -12.7) * mm});
            skPoint(sketch, "E82.11.0.2", {"position": v(24.71, -38.1) * mm});
            skLineSegment(sketch, "E82.11.0.3", {"start": v(25.98, 50.8) * mm, "end": v(28.14, 18.4) * mm});
            skLineSegment(sketch, "E82.11.0.4", {"start": v(28.9, -18.4) * mm, "end": v(31.06, -50.8) * mm});
            skLineSegment(sketch, "E82.11.0.5", {"start": v(27.25, 0) * mm, "end": v(25.1, -32.4) * mm});
            skPoint(sketch, "E82.11.0.6", {"position": v(24.71, 38.1) * mm});
            skLineSegment(sketch, "E82.11.0.7", {"start": v(27.25, 0) * mm, "end": v(25.1, 32.4) * mm});
            skLineSegment(sketch, "E82.11.0.8", {"start": v(24.71, 38.1) * mm, "end": v(24.71, 0) * mm, "construction": true});
            skLineSegment(sketch, "E82.11.0.9", {"start": v(28.9, 18.4) * mm, "end": v(31.06, 50.8) * mm});
            skLineSegment(sketch, "E82.11.0.10", {"start": v(24.33, 32.4) * mm, "end": v(22.17, 0) * mm});
            skPoint(sketch, "E82.11.0.11", {"position": v(28.52, 12.7) * mm});
            skLineSegment(sketch, "E82.11.0.12", {"start": v(28.52, 12.7) * mm, "end": v(28.52, 50.8) * mm, "construction": true});
            skLineSegment(sketch, "E82.11.0.13", {"start": v(25.98, -50.8) * mm, "end": v(28.14, -18.4) * mm});
            skLineSegment(sketch, "E82.11.0.14", {"start": v(31.06, -50.8) * mm, "end": v(25.98, -50.8) * mm});
            skArc(sketch, "E82.11.0.15", {"start": v(28.14, -18.4) * mm, "mid": v(28.52, -18.05) * mm, "end": v(28.9, -18.4) * mm});
            skLineSegment(sketch, "E82.11.0.16", {"start": v(22.17, 0) * mm, "end": v(27.25, 0) * mm, "construction": true});
            skLineSegment(sketch, "E82.11.0.17", {"start": v(31.06, 50.8) * mm, "end": v(25.98, 50.8) * mm});
            skArc(sketch, "E82.11.0.18", {"start": v(28.14, 18.4) * mm, "mid": v(28.52, 18.05) * mm, "end": v(28.9, 18.4) * mm});
            skArc(sketch, "E82.11.0.19", {"start": v(25.1, -32.4) * mm, "mid": v(24.71, -32.75) * mm, "end": v(24.33, -32.4) * mm});
            skArc(sketch, "E82.11.0.20", {"start": v(25.1, 32.4) * mm, "mid": v(24.71, 32.75) * mm, "end": v(24.33, 32.4) * mm});
            skLineSegment(sketch, "E82.12.0.0", {"start": v(31.95, -32.4) * mm, "end": v(29.8, 0) * mm});
            skPoint(sketch, "E82.12.0.1", {"position": v(36.14, -12.7) * mm});
            skPoint(sketch, "E82.12.0.2", {"position": v(32.33, -38.1) * mm});
            skLineSegment(sketch, "E82.12.0.3", {"start": v(33.6, 50.8) * mm, "end": v(35.76, 18.4) * mm});
            skLineSegment(sketch, "E82.12.0.4", {"start": v(36.52, -18.4) * mm, "end": v(38.68, -50.8) * mm});
            skLineSegment(sketch, "E82.12.0.5", {"start": v(34.87, 0) * mm, "end": v(32.71, -32.4) * mm});
            skPoint(sketch, "E82.12.0.6", {"position": v(32.33, 38.1) * mm});
            skLineSegment(sketch, "E82.12.0.7", {"start": v(34.87, 0) * mm, "end": v(32.71, 32.4) * mm});
            skLineSegment(sketch, "E82.12.0.8", {"start": v(32.33, 38.1) * mm, "end": v(32.33, 0) * mm, "construction": true});
            skLineSegment(sketch, "E82.12.0.9", {"start": v(36.52, 18.4) * mm, "end": v(38.68, 50.8) * mm});
            skLineSegment(sketch, "E82.12.0.10", {"start": v(31.95, 32.4) * mm, "end": v(29.8, 0) * mm});
            skPoint(sketch, "E82.12.0.11", {"position": v(36.14, 12.7) * mm});
            skLineSegment(sketch, "E82.12.0.12", {"start": v(36.14, 12.7) * mm, "end": v(36.14, 50.8) * mm, "construction": true});
            skLineSegment(sketch, "E82.12.0.13", {"start": v(33.6, -50.8) * mm, "end": v(35.76, -18.4) * mm});
            skLineSegment(sketch, "E82.12.0.14", {"start": v(38.68, -50.8) * mm, "end": v(33.6, -50.8) * mm});
            skArc(sketch, "E82.12.0.15", {"start": v(35.76, -18.4) * mm, "mid": v(36.14, -18.05) * mm, "end": v(36.52, -18.4) * mm});
            skLineSegment(sketch, "E82.12.0.16", {"start": v(29.8, 0) * mm, "end": v(34.87, 0) * mm, "construction": true});
            skLineSegment(sketch, "E82.12.0.17", {"start": v(38.68, 50.8) * mm, "end": v(33.6, 50.8) * mm});
            skArc(sketch, "E82.12.0.18", {"start": v(35.76, 18.4) * mm, "mid": v(36.14, 18.05) * mm, "end": v(36.52, 18.4) * mm});
            skArc(sketch, "E82.12.0.19", {"start": v(32.71, -32.4) * mm, "mid": v(32.33, -32.75) * mm, "end": v(31.95, -32.4) * mm});
            skArc(sketch, "E82.12.0.20", {"start": v(32.71, 32.4) * mm, "mid": v(32.33, 32.75) * mm, "end": v(31.95, 32.4) * mm});
            skLineSegment(sketch, "E82.13.0.0", {"start": v(39.57, -32.4) * mm, "end": v(37.41, 0) * mm});
            skPoint(sketch, "E82.13.0.1", {"position": v(43.76, -12.7) * mm});
            skPoint(sketch, "E82.13.0.2", {"position": v(39.95, -38.1) * mm});
            skLineSegment(sketch, "E82.13.0.3", {"start": v(41.22, 50.8) * mm, "end": v(43.38, 18.4) * mm});
            skLineSegment(sketch, "E82.13.0.4", {"start": v(44.14, -18.4) * mm, "end": v(46.3, -50.8) * mm});
            skLineSegment(sketch, "E82.13.0.5", {"start": v(42.5, 0) * mm, "end": v(40.33, -32.4) * mm});
            skPoint(sketch, "E82.13.0.6", {"position": v(39.95, 38.1) * mm});
            skLineSegment(sketch, "E82.13.0.7", {"start": v(42.5, 0) * mm, "end": v(40.33, 32.4) * mm});
            skLineSegment(sketch, "E82.13.0.8", {"start": v(39.95, 38.1) * mm, "end": v(39.95, 0) * mm, "construction": true});
            skLineSegment(sketch, "E82.13.0.9", {"start": v(44.14, 18.4) * mm, "end": v(46.3, 50.8) * mm});
            skLineSegment(sketch, "E82.13.0.10", {"start": v(39.57, 32.4) * mm, "end": v(37.41, 0) * mm});
            skPoint(sketch, "E82.13.0.11", {"position": v(43.76, 12.7) * mm});
            skLineSegment(sketch, "E82.13.0.12", {"start": v(43.76, 12.7) * mm, "end": v(43.76, 50.8) * mm, "construction": true});
            skLineSegment(sketch, "E82.13.0.13", {"start": v(41.22, -50.8) * mm, "end": v(43.38, -18.4) * mm});
            skLineSegment(sketch, "E82.13.0.14", {"start": v(46.3, -50.8) * mm, "end": v(41.22, -50.8) * mm});
            skArc(sketch, "E82.13.0.15", {"start": v(43.38, -18.4) * mm, "mid": v(43.76, -18.05) * mm, "end": v(44.14, -18.4) * mm});
            skLineSegment(sketch, "E82.13.0.16", {"start": v(37.41, 0) * mm, "end": v(42.5, 0) * mm, "construction": true});
            skLineSegment(sketch, "E82.13.0.17", {"start": v(46.3, 50.8) * mm, "end": v(41.22, 50.8) * mm});
            skArc(sketch, "E82.13.0.18", {"start": v(43.38, 18.4) * mm, "mid": v(43.76, 18.05) * mm, "end": v(44.14, 18.4) * mm});
            skArc(sketch, "E82.13.0.19", {"start": v(40.33, -32.4) * mm, "mid": v(39.95, -32.75) * mm, "end": v(39.57, -32.4) * mm});
            skArc(sketch, "E82.13.0.20", {"start": v(40.33, 32.4) * mm, "mid": v(39.95, 32.75) * mm, "end": v(39.57, 32.4) * mm});
            skLineSegment(sketch, "E82.14.0.0", {"start": v(47.2, -32.4) * mm, "end": v(45.03, 0) * mm});
            skPoint(sketch, "E82.14.0.1", {"position": v(51.38, -12.7) * mm});
            skPoint(sketch, "E82.14.0.2", {"position": v(47.57, -38.1) * mm});
            skLineSegment(sketch, "E82.14.0.3", {"start": v(48.84, 50.8) * mm, "end": v(51, 18.4) * mm});
            skLineSegment(sketch, "E82.14.0.4", {"start": v(51.76, -18.4) * mm, "end": v(53.92, -50.8) * mm});
            skLineSegment(sketch, "E82.14.0.5", {"start": v(50.11, 0) * mm, "end": v(47.95, -32.4) * mm});
            skPoint(sketch, "E82.14.0.6", {"position": v(47.57, 38.1) * mm});
            skLineSegment(sketch, "E82.14.0.7", {"start": v(50.11, 0) * mm, "end": v(47.95, 32.4) * mm});
            skLineSegment(sketch, "E82.14.0.8", {"start": v(47.57, 38.1) * mm, "end": v(47.57, 0) * mm, "construction": true});
            skLineSegment(sketch, "E82.14.0.9", {"start": v(51.76, 18.4) * mm, "end": v(53.92, 50.8) * mm});
            skLineSegment(sketch, "E82.14.0.10", {"start": v(47.2, 32.4) * mm, "end": v(45.03, 0) * mm});
            skPoint(sketch, "E82.14.0.11", {"position": v(51.38, 12.7) * mm});
            skLineSegment(sketch, "E82.14.0.12", {"start": v(51.38, 12.7) * mm, "end": v(51.38, 50.8) * mm, "construction": true});
            skLineSegment(sketch, "E82.14.0.13", {"start": v(48.84, -50.8) * mm, "end": v(51, -18.4) * mm});
            skLineSegment(sketch, "E82.14.0.14", {"start": v(53.92, -50.8) * mm, "end": v(48.84, -50.8) * mm});
            skArc(sketch, "E82.14.0.15", {"start": v(51, -18.4) * mm, "mid": v(51.38, -18.05) * mm, "end": v(51.76, -18.4) * mm});
            skLineSegment(sketch, "E82.14.0.16", {"start": v(45.03, 0) * mm, "end": v(50.11, 0) * mm, "construction": true});
            skLineSegment(sketch, "E82.14.0.17", {"start": v(53.92, 50.8) * mm, "end": v(48.84, 50.8) * mm});
            skArc(sketch, "E82.14.0.18", {"start": v(51, 18.4) * mm, "mid": v(51.38, 18.05) * mm, "end": v(51.76, 18.4) * mm});
            skArc(sketch, "E82.14.0.19", {"start": v(47.95, -32.4) * mm, "mid": v(47.57, -32.75) * mm, "end": v(47.2, -32.4) * mm});
            skArc(sketch, "E82.14.0.20", {"start": v(47.95, 32.4) * mm, "mid": v(47.57, 32.75) * mm, "end": v(47.2, 32.4) * mm});
            skLineSegment(sketch, "E82.direction1", {"start": v(-57.84, -50.8) * mm, "end": v(-50.22, -50.8) * mm, "construction": true});
            skSolve(sketch);
        }
        {
            var Q0;
            Q0 = qSketchRegion(id + "F2", true);
            extrude(context, id + "F3", {"entities" : qUnion([Q0]), "operationType" : NewBodyOperationType.REMOVE, "endBound" : BoundingType.THROUGH_ALL, "oppositeDirection" : true, "depth" : 25.4 * mm, "offsetDistance" : 25.4 * mm});
        }
    });
